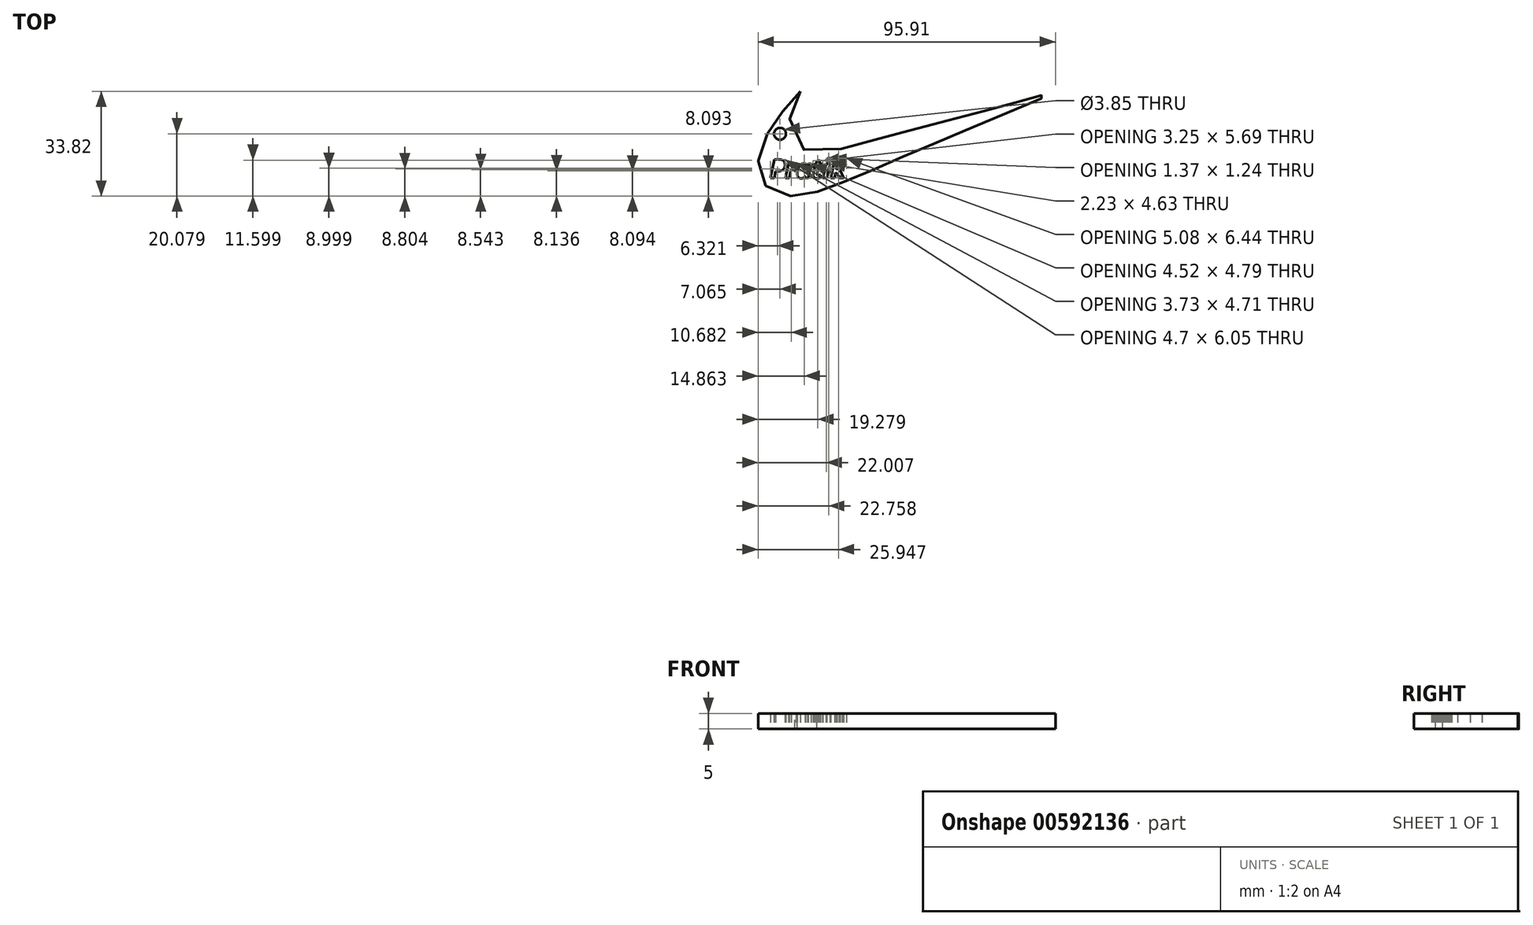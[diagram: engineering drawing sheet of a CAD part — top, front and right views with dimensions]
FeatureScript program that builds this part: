
annotation { "Feature Type Name" : "Feature", "Feature Type Description" : "" }
export const myFeature = defineFeature(function(context is Context, id is Id, definition is map)
    precondition{}
    {
        {
            var Q0;
            Q0=qCreatedBy(makeId("Top.planeOp"),FACE);
            var sketch = newSketch(context, id + "F0", { "sketchPlane" : qUnion([Q0])});
            skPoint(sketch, "E0.166.internal.snap0", {"position": v(-53.04, 14.06) * mm});
            skFitSpline(sketch, "E0", {"points": [v(-33.35, 29.44) * mm, v(-33.7, 29.05) * mm, v(-34.2, 28.46) * mm, v(-35.02, 27.62) * mm, v(-35.74, 26.8) * mm, v(-36.56, 25.84) * mm, v(-37.03, 25.3) * mm, v(-37.49, 24.84) * mm, v(-38, 24.15) * mm, v(-38.89, 23.12) * mm, v(-39.6, 22.2) * mm, v(-39.99, 21.66) * mm, v(-40.6, 20.95) * mm, v(-41.2, 20.1) * mm, v(-41.7, 19.34) * mm, v(-42.23, 18.6) * mm, v(-42.8, 17.63) * mm, v(-43.41, 16.77) * mm, v(-43.98, 15.7) * mm, v(-44.38, 14.98) * mm, v(-45.05, 13.56) * mm, v(-45.52, 12.52) * mm, v(-45.73, 11.77) * mm, v(-46.05, 10.95) * mm, v(-46.38, 9.8) * mm, v(-46.66, 8.42) * mm, v(-46.8, 7.7) * mm, v(-46.91, 6.67) * mm, v(-46.95, 5.52) * mm, v(-46.91, 4.35) * mm, v(-46.8, 3.6) * mm, v(-46.66, 2.88) * mm, v(-46.3, 1.77) * mm, v(-45.79, 0.78) * mm, v(-45.52, 0.22) * mm, v(-44.98, -0.4) * mm, v(-44.32, -1.3) * mm, v(-43.49, -2) * mm, v(-42.82, -2.54) * mm, v(-42.18, -2.91) * mm, v(-41.56, -3.23) * mm, v(-40.66, -3.55) * mm, v(-39.61, -3.93) * mm, v(-38.47, -4.16) * mm, v(-37.26, -4.25) * mm, v(-36.37, -4.35) * mm, v(-35.16, -4.38) * mm, v(-34.24, -4.35) * mm, v(-33.54, -4.22) * mm, v(-32, -3.98) * mm, v(-31.3, -3.89) * mm, v(-30.36, -3.7) * mm, v(-29.33, -3.46) * mm, v(-28.47, -3.21) * mm, v(-27.55, -2.99) * mm, v(-26.7, -2.72) * mm, v(-25.95, -2.45) * mm, v(-25.03, -2.18) * mm, v(-24.24, -1.84) * mm, v(-22.7, -1.23) * mm, v(-21.59, -0.76) * mm, v(-20.55, -0.33) * mm, v(-19.83, 0) * mm, v(-18.87, 0.39) * mm, v(-17.79, 0.81) * mm, v(-16.55, 1.4) * mm, v(-15.02, 2.03) * mm, v(-13.78, 2.55) * mm, v(-12.9, 2.9) * mm, v(-11.32, 3.47) * mm, v(-10.5, 3.87) * mm, v(-9.22, 4.4) * mm, v(-8.22, 4.9) * mm, v(-6.9, 5.44) * mm, v(-6.06, 5.79) * mm, v(-4, 6.62) * mm, v(-2.52, 7.3) * mm, v(-1.04, 7.87) * mm, v(0, 8.37) * mm, v(1.32, 8.88) * mm, v(2.5, 9.38) * mm, v(3.71, 9.89) * mm, v(5.06, 10.46) * mm, v(6.54, 11.1) * mm, v(8.26, 11.84) * mm, v(9.68, 12.45) * mm, v(10.92, 12.99) * mm, v(12.4, 13.6) * mm, v(13.72, 14.13) * mm, v(15.07, 14.74) * mm, v(17.02, 15.51) * mm, v(18.37, 16.13) * mm, v(19.79, 16.74) * mm, v(21.86, 17.63) * mm, v(23.36, 18.28) * mm, v(24.9, 18.85) * mm, v(27.2, 19.76) * mm, v(29.23, 20.67) * mm, v(31.16, 21.47) * mm, v(33.46, 22.48) * mm, v(35.92, 23.5) * mm, v(38.16, 24.46) * mm, v(40.36, 25.48) * mm, v(42.5, 26.39) * mm, v(44.58, 27.2) * mm, v(47.1, 28.37) * mm, v(48.43, 28.89) * mm, v(48.93, 29.1) * mm, v(48.95, 29.17) * mm, v(48.4, 29.08) * mm, v(47.66, 28.86) * mm, v(46.59, 28.56) * mm, v(45.78, 28.4) * mm, v(44.7, 28.14) * mm, v(43.41, 27.75) * mm, v(42.31, 27.44) * mm, v(41.25, 27.15) * mm, v(40.06, 26.88) * mm, v(39.19, 26.63) * mm, v(38.26, 26.36) * mm, v(37.32, 26.11) * mm, v(36.5, 25.89) * mm, v(35.56, 25.64) * mm, v(33.95, 25.2) * mm, v(32.62, 24.83) * mm, v(31.36, 24.52) * mm, v(30.19, 24.2) * mm, v(29, 23.89) * mm, v(27.72, 23.53) * mm, v(26.41, 23.19) * mm, v(25.2, 22.9) * mm, v(23.87, 22.56) * mm, v(22.36, 22.1) * mm, v(21.04, 21.8) * mm, v(18.46, 21.13) * mm, v(16.35, 20.52) * mm, v(14.4, 20.02) * mm, v(12.1, 19.41) * mm, v(10.07, 18.88) * mm, v(7.75, 18.27) * mm, v(6.1, 17.84) * mm, v(4.29, 17.34) * mm, v(2.64, 16.91) * mm, v(1.22, 16.52) * mm, v(0, 16.2) * mm, v(-1.18, 15.84) * mm, v(-2.46, 15.52) * mm, v(-3.92, 15.17) * mm, v(-5.39, 14.77) * mm, v(-6.82, 14.38) * mm, v(-8.2, 14.02) * mm, v(-11.1, 13.2) * mm, v(-12.92, 12.77) * mm, v(-14.58, 12.35) * mm, v(-16.3, 11.86) * mm, v(-17.9, 11.44) * mm, v(-19.82, 10.95) * mm, v(-22.07, 10.31) * mm, v(-23.94, 10.05) * mm, v(-25.7, 9.78) * mm, v(-28.06, 9.72) * mm, v(-29.93, 9.88) * mm, v(-31.21, 10.15) * mm, v(-32.93, 10.9) * mm, v(-34.21, 11.86) * mm, v(-35.28, 13.25) * mm, v(-35.87, 14.06) * mm, v(-36.62, 15.82) * mm, v(-36.83, 17.75) * mm, v(-36.88, 19.89) * mm, v(-36.4, 22.08) * mm, v(-35.98, 23.8) * mm, v(-35.23, 25.77) * mm, v(-34.32, 27.64) * mm, v(-34.14, 28.02) * mm, v(-33.93, 28.36) * mm, v(-33.7, 28.73) * mm, v(-33.5, 29.11) * mm, v(-33.25, 29.38) * mm, v(-33.35, 29.44) * mm]});
            skText(sketch, "E1", { "text": "Pratik\n", "fontName": "OpenSans-BoldItalic.ttf"});
            skCircle(sketch, "E2", {"center": v(-39.89, 15.7) * mm, "radius": 1.93 * mm});
            const initialGuessF0  = {"E1": [-0.0432, 0.0014, 1, 0, 0.0061]};
            skSetInitialGuess(sketch, initialGuessF0);
            skSolve(sketch);
        }
        {
            var Q0;
            Q0=makeQuery(id+"F0.imprint","IMPRINT",FACE,{"disambiguationData":[TD([[makeQuery(id+"F0.imprint","IMPRINT",EDGE,{"derivedFrom":sQuery(id+"F0.wireOp",EDGE,"E0")}),1.0]])]});
            extrude(context, id + "F1", {"entities" : qUnion([Q0]), "depth" : 5 * mm, "offsetDistance" : 25 * mm});
        }
        {
            var Q0;
            Q0 = qSketchRegion(id + "F0", true);
            extrude(context, id + "F2", {"entities" : qUnion([Q0]), "operationType" : NewBodyOperationType.ADD, "depth" : 5 * mm, "offsetDistance" : 25 * mm});
        }
    });
